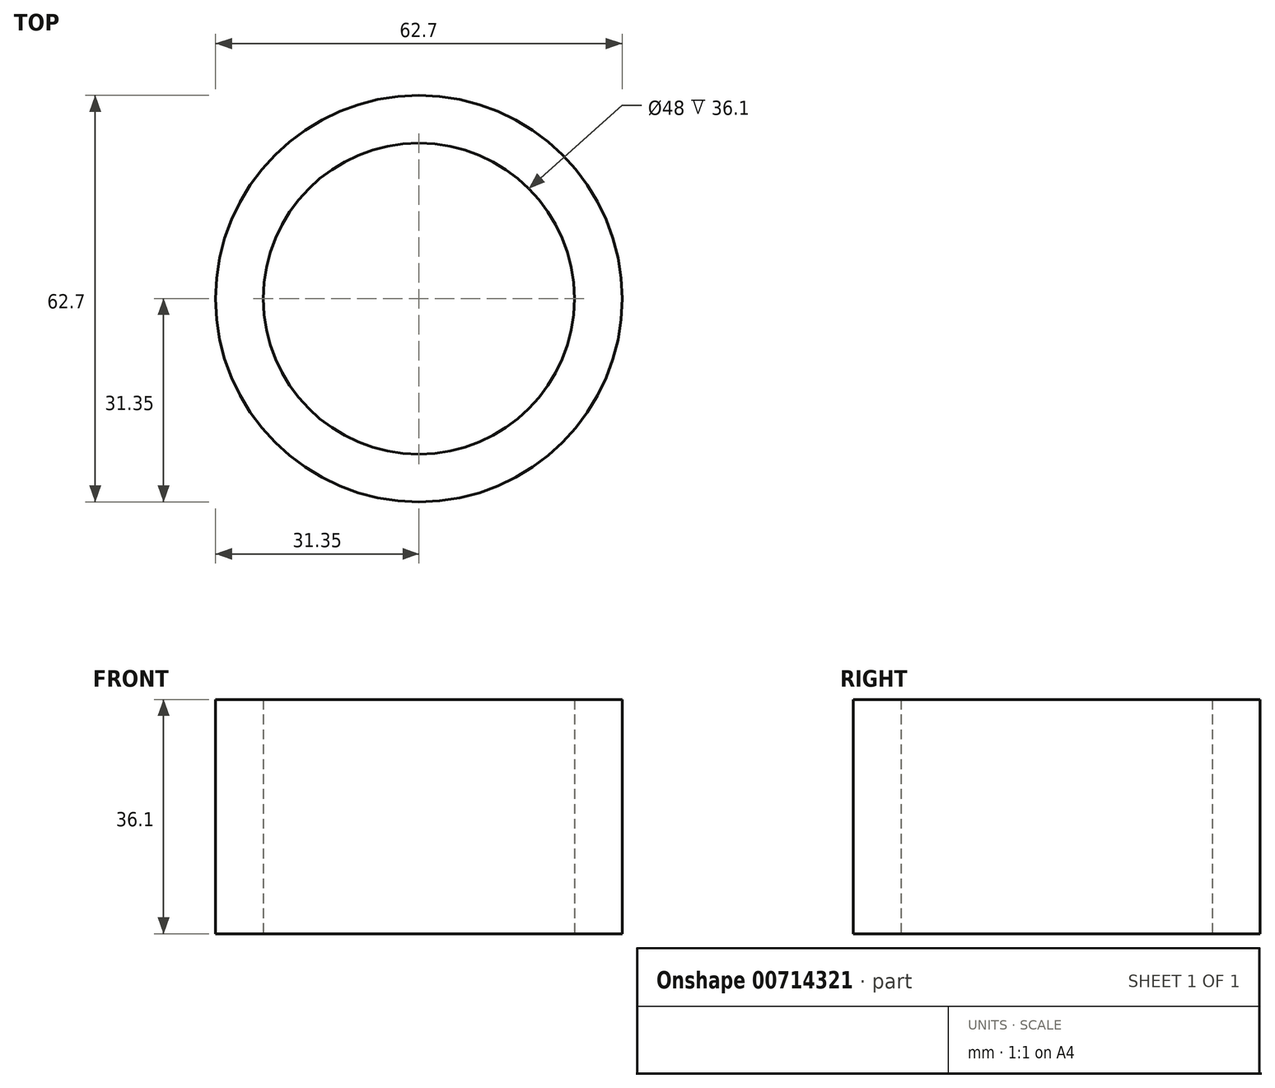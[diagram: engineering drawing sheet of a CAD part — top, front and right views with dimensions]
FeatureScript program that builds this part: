
annotation { "Feature Type Name" : "Feature", "Feature Type Description" : "" }
export const myFeature = defineFeature(function(context is Context, id is Id, definition is map)
    precondition{}
    {
        {
            var Q0;
            Q0=qCreatedBy(makeId("Top.planeOp"),FACE);
            var sketch = newSketch(context, id + "F0", { "sketchPlane" : qUnion([Q0])});
            skCircle(sketch, "E0", {"center": v(0, 0) * mm, "radius": 24 * mm});
            skCircle(sketch, "E1", {"center": v(0, 0) * mm, "radius": 31.35 * mm});
            skSolve(sketch);
        }
        {
            var Q0;
            Q0=makeQuery(id+"F0.imprint","IMPRINT",FACE,{"disambiguationData":[TD([[makeQuery(id+"F0.imprint","IMPRINT",EDGE,{"derivedFrom":sQuery(id+"F0.wireOp",EDGE,"E0")}),-1.0]])]});
            extrude(context, id + "F1", {"entities" : qUnion([Q0]), "depth" : 36.1 * mm, "offsetDistance" : 25 * mm});
        }
    });
